# Revit family: FU_Stool_Sandler_RiverSnake_903_10
name_source: partatom
category: Furniture
units: mm (PartAtom-declared; Revit-internal decimal feet)

## family parameters
Always vertical = Yes
Cut with Voids When Loaded = No
OmniClass Number = 23.40.20.00
OmniClass Title = General Furniture and Specialties
Room Calculation Point = No
Shared = No
Work Plane-Based = No

## types (1)
- Riversnake 903.10
    Default Elevation = 0 mm  [stored 0 ft]
    Depth = 480 mm  [stored 1.5748 ft]
    Description = Stool in low density polyurethane, with aluminium linking system. For indoor and outdoor use. Minimum order quantity for custom colours 20pcs.
    Height = 445 mm  [stored 1.45997 ft]
    Integral Foam = Integral Foam - X19 Pigeon Blue
    Manufacturer = Sandler
    Model = Riversnake 903.10
    URL = https://www.sandlerseating.com
    Width = 640 mm  [stored 2.09974 ft]

note: [stored X ft] marks values corroborated as IEEE doubles in the binary element streams (Revit-internal decimal feet)

## geometry (parser evidence)
native form markers: Sweep x4
no freeform markers — native parametric forms only
